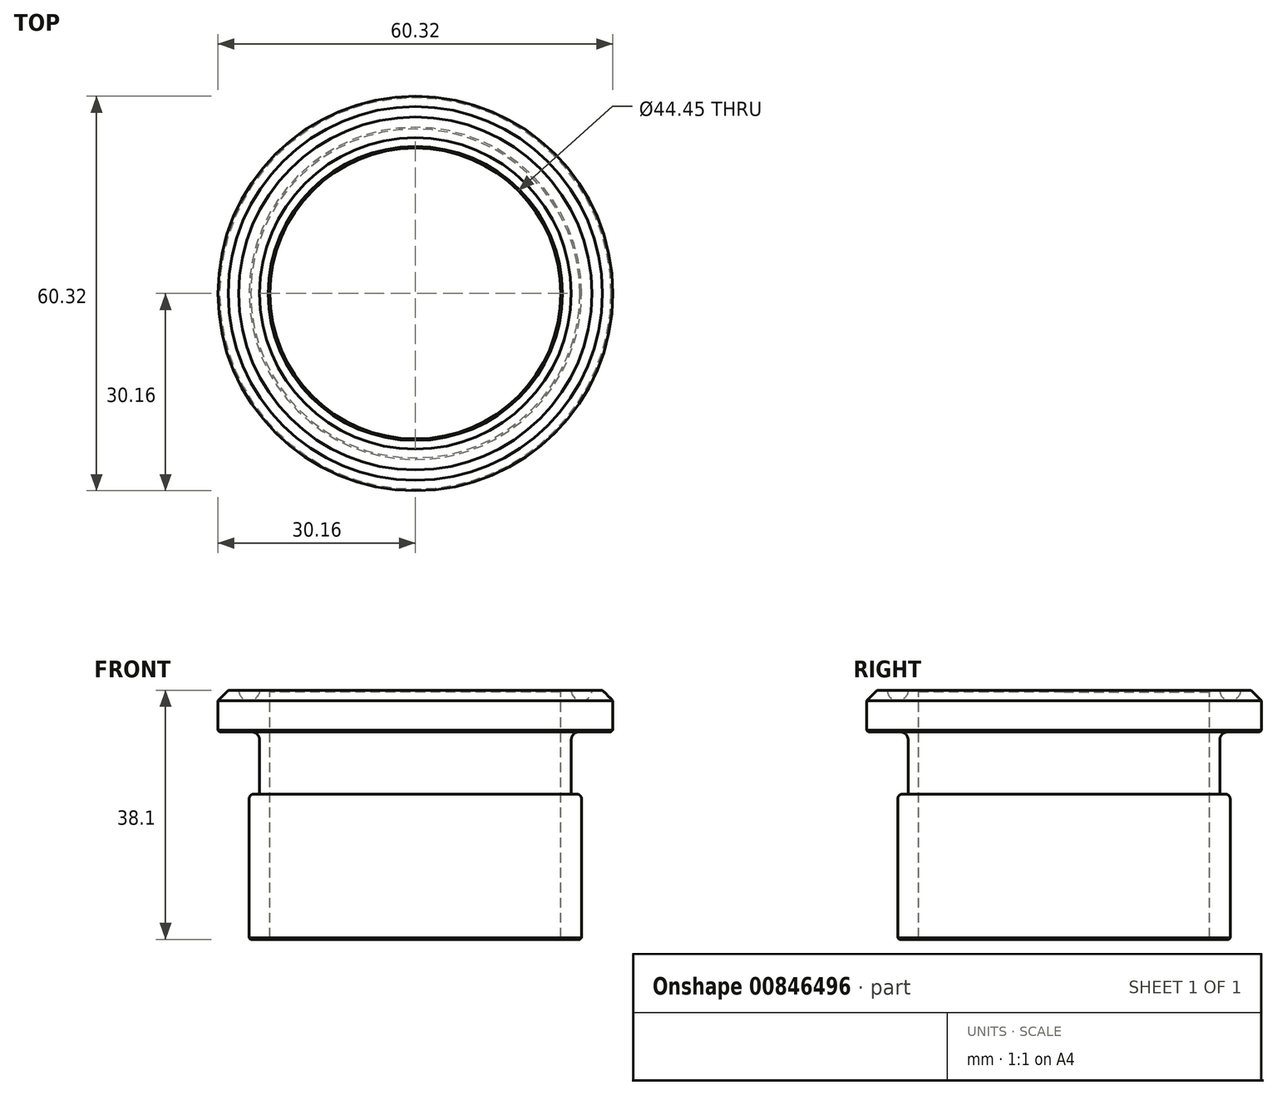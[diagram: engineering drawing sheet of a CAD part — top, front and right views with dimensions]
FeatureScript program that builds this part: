
annotation { "Feature Type Name" : "Feature", "Feature Type Description" : "" }
export const myFeature = defineFeature(function(context is Context, id is Id, definition is map)
    precondition{}
    {
        {
            var Q0;
            Q0=qCreatedBy(makeId("Front.planeOp"),FACE);
            var sketch = newSketch(context, id + "F0", { "sketchPlane" : qUnion([Q0])});
            skLineSegment(sketch, "E0", {"start": v(-22.23, 0) * mm, "end": v(-22.22, -38.1) * mm});
            skLineSegment(sketch, "E1", {"start": v(-22.22, -38.1) * mm, "end": v(-25.4, -38.1) * mm});
            skLineSegment(sketch, "E2", {"start": v(-25.4, -38.1) * mm, "end": v(-25.4, -16.64) * mm});
            skLineSegment(sketch, "E3", {"start": v(-24.64, -15.88) * mm, "end": v(-23.81, -15.88) * mm});
            skLineSegment(sketch, "E4", {"start": v(-23.81, -15.88) * mm, "end": v(-23.81, -6.35) * mm});
            skLineSegment(sketch, "E5", {"start": v(-23.81, -6.35) * mm, "end": v(-30.16, -6.35) * mm});
            skLineSegment(sketch, "E6", {"start": v(-30.16, -6.35) * mm, "end": v(-30.16, -1.59) * mm});
            skLineSegment(sketch, "E7", {"start": v(-30.16, -1.59) * mm, "end": v(-28.58, 0) * mm});
            skLineSegment(sketch, "E8", {"start": v(-28.58, 0) * mm, "end": v(-26.99, 0) * mm});
            skArc(sketch, "E9", {"start": v(-26.99, 0) * mm, "mid": v(-25.4, -1.59) * mm, "end": v(-23.81, 0) * mm});
            skLineSegment(sketch, "E10.trimOffspring", {"start": v(-23.81, 0) * mm, "end": v(-22.23, 0) * mm});
            skLineSegment(sketch, "E11", {"start": v(0, 14.14) * mm, "end": v(0, -44.43) * mm, "construction": true});
            skPoint(sketch, "E12.visualSharp", {"position": v(-25.4, -15.88) * mm});
            skArc(sketch, "E12.filletArc", {"start": v(-24.64, -15.88) * mm, "mid": v(-25.18, -16.1) * mm, "end": v(-25.4, -16.64) * mm});
            skSolve(sketch);
        }
        {
            var Q0;
            Q0=makeQuery(id+"F0.imprint","IMPRINT",FACE,{"disambiguationData":[TD([[makeQuery(id+"F0.imprint","IMPRINT",EDGE,{"derivedFrom":sQuery(id+"F0.wireOp",EDGE,"E0")}),-1.0]])]});
            var Q1;
            Q1=sQuery(id+"F0.wireOp",EDGE,"E11");
            revolve(context, id + "F1", {"surfaceOperationType" : NewSurfaceOperationType.NEW, "entities" : qUnion([Q0]), "axis" : qUnion([Q1]), "revolveType" : RevolveType.FULL});
        }
        {
            var Q0;
            Q0=makeQuery(id+"F1.opRevolve","SWEPT_EDGE",EDGE,{"disambiguationData":[OSD([sQuery(id+"F0.wireOp",EDGE,"E4"),sQuery(id+"F0.wireOp",EDGE,"E5")])]});
            fillet(context, id + "F2", {"entities" : qUnion([Q0]), "radius" : 1.27 * mm, "tangentPropagation" : true, "allowEdgeOverflow" : false});
        }
        {
            var Q0;
            Q0=makeQuery(id+"F1.opRevolve","SWEPT_EDGE",EDGE,{"disambiguationData":[OSD([sQuery(id+"F0.wireOp",EDGE,"E5"),sQuery(id+"F0.wireOp",EDGE,"E6")])]});
            var Q1;
            Q1=makeQuery(id+"F1.opRevolve","SWEPT_EDGE",EDGE,{"disambiguationData":[OSD([sQuery(id+"F0.wireOp",EDGE,"E1"),sQuery(id+"F0.wireOp",EDGE,"E2")])]});
            var Q2;
            Q2=makeQuery(id+"F1.opRevolve","SWEPT_EDGE",EDGE,{"disambiguationData":[OSD([sQuery(id+"F0.wireOp",EDGE,"E0"),sQuery(id+"F0.wireOp",EDGE,"E10.trimOffspring")])]});
            var Q3;
            Q3=makeQuery(id+"F1.opRevolve","SWEPT_EDGE",EDGE,{"disambiguationData":[OSD([sQuery(id+"F0.wireOp",EDGE,"E0"),sQuery(id+"F0.wireOp",EDGE,"E1")])]});
            chamfer(context, id + "F3", {"entities" : qUnion([Q0, Q1, Q2, Q3]), "width" : 0.25 * mm, "tangentPropagation" : true});
        }
    });
